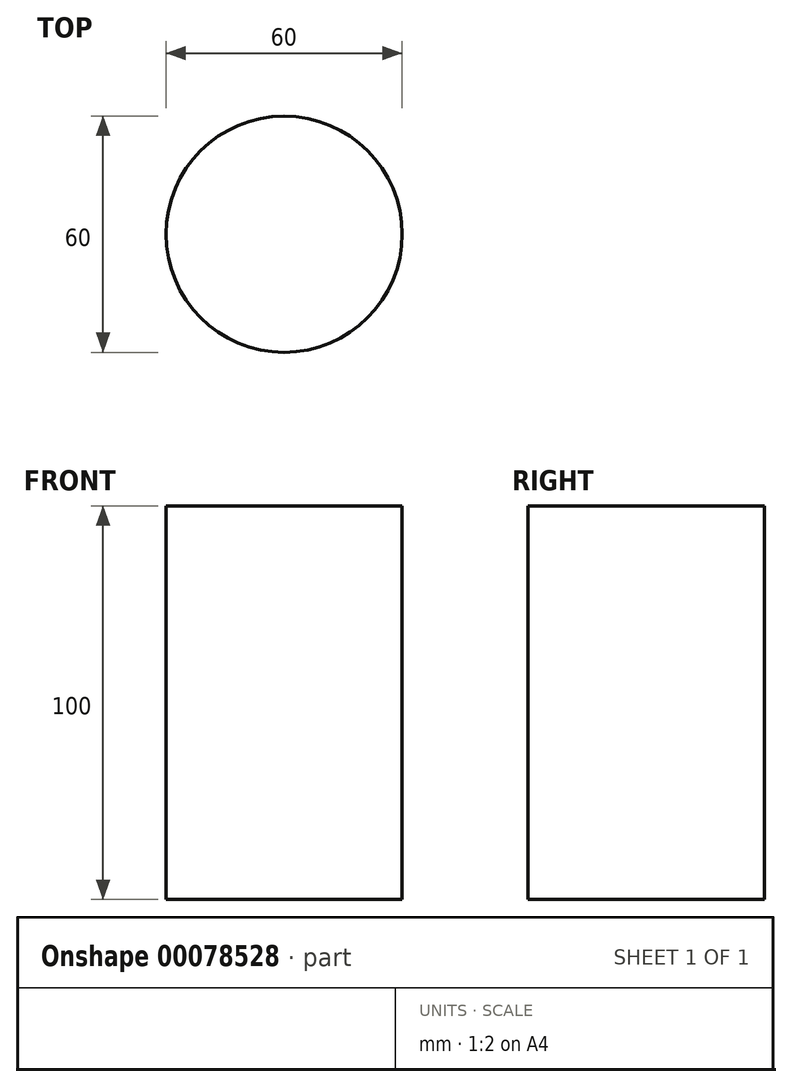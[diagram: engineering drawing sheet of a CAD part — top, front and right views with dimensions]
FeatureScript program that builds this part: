
annotation { "Feature Type Name" : "Feature", "Feature Type Description" : "" }
export const myFeature = defineFeature(function(context is Context, id is Id, definition is map)
    precondition{}
    {
        {
            var Q0;
            Q0=qCreatedBy(makeId("Right.planeOp"),FACE);
            var sketch = newSketch(context, id + "F0", { "sketchPlane" : qUnion([Q0])});
            skLineSegment(sketch, "E0.bottom", {"start": v(0, 0) * mm, "end": v(30, 0) * mm});
            skLineSegment(sketch, "E0.top", {"start": v(0, 100) * mm, "end": v(30, 100) * mm});
            skLineSegment(sketch, "E0.left", {"start": v(0, 0) * mm, "end": v(0, 100) * mm});
            skLineSegment(sketch, "E0.right", {"start": v(30, 0) * mm, "end": v(30, 100) * mm});
            skLineSegment(sketch, "E1", {"start": v(0, -38.37) * mm, "end": v(0, 114.43) * mm, "construction": true});
            skSolve(sketch);
        }
        {
            var Q0;
            Q0=makeQuery(id+"F0.imprint","IMPRINT",FACE,{"disambiguationData":[TD([[makeQuery(id+"F0.imprint","IMPRINT",EDGE,{"derivedFrom":sQuery(id+"F0.wireOp",EDGE,"E0.bottom")}),1.0]])]});
            var Q1;
            Q1=sQuery(id+"F0.wireOp",EDGE,"E1");
            revolve(context, id + "F1", {"entities" : qUnion([Q0]), "axis" : qUnion([Q1]), "revolveType" : RevolveType.FULL});
        }
    });
